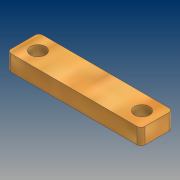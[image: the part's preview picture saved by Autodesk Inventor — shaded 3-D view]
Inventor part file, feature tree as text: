
AUTODESK INVENTOR PART (.ipt)
format: ipt  version: 2021 (Build 250183000, 183)  size: 122,880 bytes
history: native  units: mm
features: extrude x1, fillet x1, sketch x1
ambient origin geometry x8: Origin, YZ Plane, XZ Plane, XY Plane, X Axis, Y Axis, Z Axis, Center Point
bodies: Solid1 (feature_tree)
feature tree (3):
  extrude  "Extrusion1"  Depth=67.0mm
  fillet  "Fillet1"  Radius=52.0mm
  sketch  "Sketch1"  dims[d0=16.0mm d1=67.0mm d2=52.0mm d3=7.5mm d4=8.0mm d5=0.0mm d6=2.0mm]
